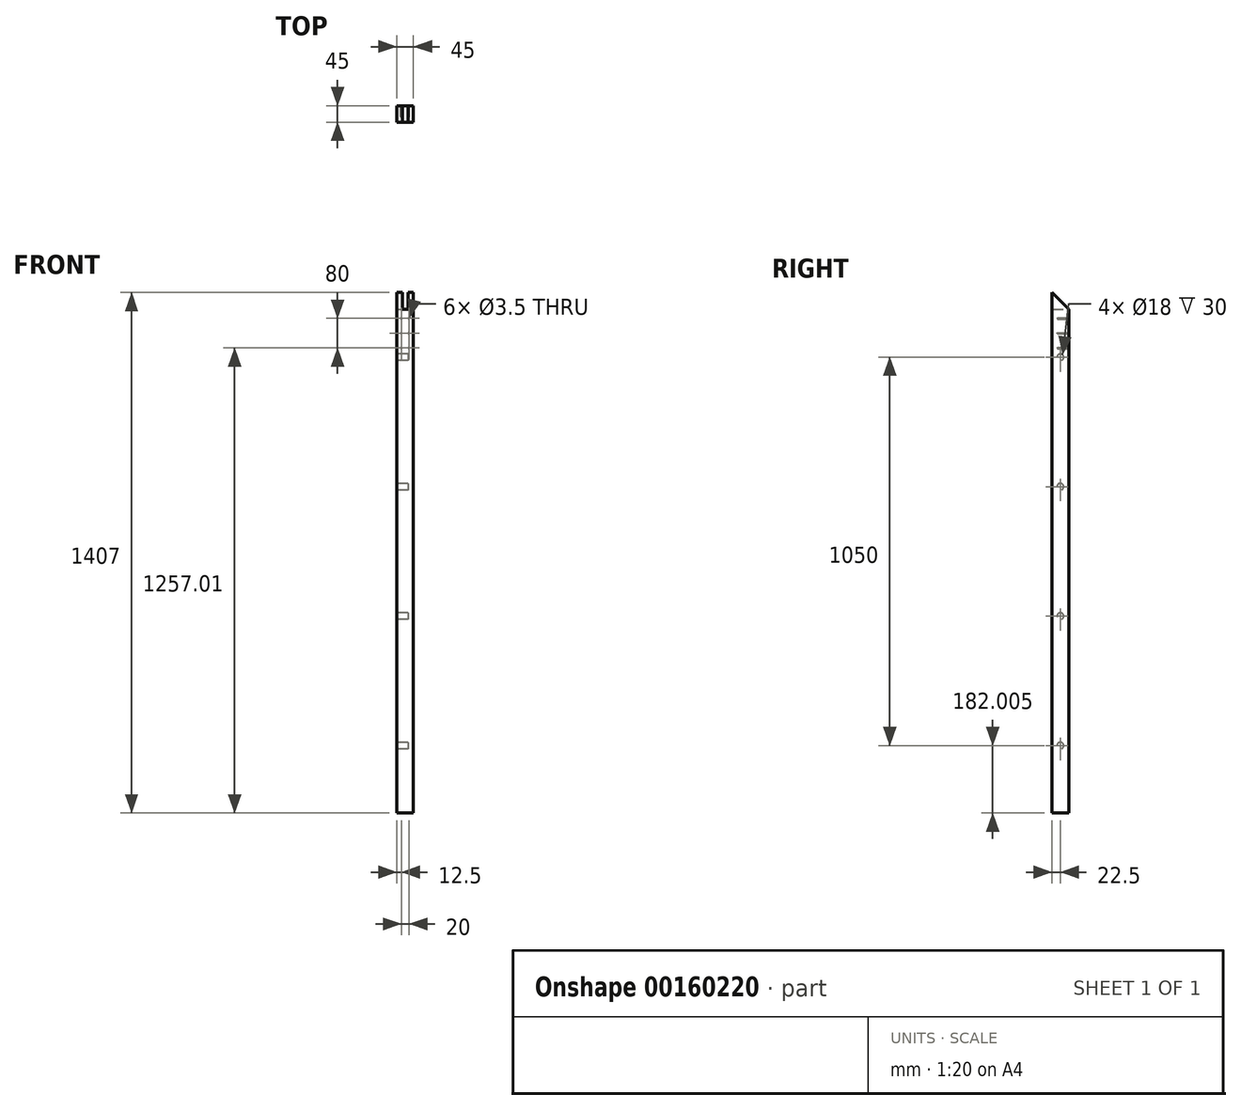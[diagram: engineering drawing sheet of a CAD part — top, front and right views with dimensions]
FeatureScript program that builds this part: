
annotation { "Feature Type Name" : "Feature", "Feature Type Description" : "" }
export const myFeature = defineFeature(function(context is Context, id is Id, definition is map)
    precondition{}
    {
        {
            var Q0;
            Q0=qCreatedBy(makeId("Front.planeOp"),FACE);
            var sketch = newSketch(context, id + "F0", { "sketchPlane" : qUnion([Q0])});
            skLineSegment(sketch, "E0.bottom", {"start": v(-22.5, 213.33) * mm, "end": v(22.5, 213.33) * mm});
            skLineSegment(sketch, "E0.top", {"start": v(-22.5, -1193.67) * mm, "end": v(22.5, -1193.67) * mm});
            skLineSegment(sketch, "E0.left", {"start": v(-22.5, 213.33) * mm, "end": v(-22.5, -1193.67) * mm});
            skLineSegment(sketch, "E0.right", {"start": v(22.5, 213.33) * mm, "end": v(22.5, -1193.67) * mm});
            skSolve(sketch);
        }
        {
            var Q0;
            Q0=makeQuery(id+"F0.imprint","IMPRINT",FACE,{"disambiguationData":[TD([[makeQuery(id+"F0.imprint","IMPRINT",EDGE,{"derivedFrom":sQuery(id+"F0.wireOp",EDGE,"E0.bottom")}),-1.0]])]});
            extrude(context, id + "F1", {"entities" : qUnion([Q0]), "endBound" : BoundingType.SYMMETRIC, "depth" : 45 * mm});
        }
        {
            var Q0;
            Q0=makeQuery(id+"F1.opExtrude","SWEPT_FACE",FACE,{"disambiguationData":[OSD([sQuery(id+"F0.wireOp",EDGE,"E0.bottom")])]});
            var sketch = newSketch(context, id + "F2", { "sketchPlane" : qUnion([Q0])});
            skLineSegment(sketch, "E1.bottom", {"start": v(7.5, -22.5) * mm, "end": v(22.5, -22.5) * mm});
            skLineSegment(sketch, "E1.top", {"start": v(7.5, 22.5) * mm, "end": v(22.5, 22.5) * mm});
            skLineSegment(sketch, "E1.left", {"start": v(7.5, -22.5) * mm, "end": v(7.5, 22.5) * mm});
            skLineSegment(sketch, "E1.right", {"start": v(22.5, -22.5) * mm, "end": v(22.5, 22.5) * mm});
            skLineSegment(sketch, "E2.bottom", {"start": v(-7.5, -22.5) * mm, "end": v(-22.5, -22.5) * mm});
            skLineSegment(sketch, "E2.top", {"start": v(-7.5, 22.5) * mm, "end": v(-22.5, 22.5) * mm});
            skLineSegment(sketch, "E2.left", {"start": v(-7.5, -22.5) * mm, "end": v(-7.5, 22.5) * mm});
            skLineSegment(sketch, "E2.right", {"start": v(-22.5, -22.5) * mm, "end": v(-22.5, 22.5) * mm});
            skSolve(sketch);
        }
        {
            var Q0;
            Q0=makeQuery(id+"F1.opExtrude","CAP_EDGE",EDGE,{"disambiguationData":[OSD([sQuery(id+"F0.wireOp",EDGE,"E0.bottom")])],"isStart":true});
            chamfer(context, id + "F3", {"entities" : qUnion([Q0]), "chamferType" : ChamferType.OFFSET_ANGLE, "width" : 45 * mm, "oppositeDirection" : false, "angle" : 45 * degree, "tangentPropagation" : true});
        }
        {
            var Q0;
            {var subQ0=sQuery(id+"F2.wireOp",EDGE,"E1.left");Q0=makeQuery(id+"F2.imprint","IMPRINT",FACE,{"disambiguationData":[TD([[makeQuery(id+"F2.imprint","IMPRINT",EDGE,{"derivedFrom":subQ0}),1.0]])]});}
            extrude(context, id + "F4", {"entities" : qUnion([Q0]), "operationType" : NewBodyOperationType.REMOVE, "oppositeDirection" : true, "depth" : 45 * mm});
        }
        {
            var Q0;
            Q0=makeQuery(id+"F1.opExtrude","SWEPT_FACE",FACE,{"disambiguationData":[OSD([sQuery(id+"F0.wireOp",EDGE,"E0.left")])]});
            var sketch = newSketch(context, id + "F5", { "sketchPlane" : qUnion([Q0])});
            skCircle(sketch, "E3", {"center": v(0, 38.33) * mm, "radius": 9 * mm});
            skCircle(sketch, "E4", {"center": v(0, -311.67) * mm, "radius": 9 * mm});
            skCircle(sketch, "E5", {"center": v(0, -661.67) * mm, "radius": 9 * mm});
            skCircle(sketch, "E6", {"center": v(0, -1011.67) * mm, "radius": 9 * mm});
            skSolve(sketch);
        }
        {
            var Q0;
            Q0=makeQuery(id+"F5.imprint","IMPRINT",FACE,{"disambiguationData":[TD([[makeQuery(id+"F5.imprint","IMPRINT",EDGE,{"derivedFrom":sQuery(id+"F5.wireOp",EDGE,"E3")}),1.0]])]});
            var Q1;
            Q1=makeQuery(id+"F5.imprint","IMPRINT",FACE,{"disambiguationData":[TD([[makeQuery(id+"F5.imprint","IMPRINT",EDGE,{"derivedFrom":sQuery(id+"F5.wireOp",EDGE,"E4")}),1.0]])]});
            var Q2;
            Q2=makeQuery(id+"F5.imprint","IMPRINT",FACE,{"disambiguationData":[TD([[makeQuery(id+"F5.imprint","IMPRINT",EDGE,{"derivedFrom":sQuery(id+"F5.wireOp",EDGE,"E5")}),1.0]])]});
            var Q3;
            Q3=makeQuery(id+"F5.imprint","IMPRINT",FACE,{"disambiguationData":[TD([[makeQuery(id+"F5.imprint","IMPRINT",EDGE,{"derivedFrom":sQuery(id+"F5.wireOp",EDGE,"E6")}),1.0]])]});
            extrude(context, id + "F6", {"entities" : qUnion([Q0, Q1, Q2, Q3]), "operationType" : NewBodyOperationType.REMOVE, "oppositeDirection" : true, "depth" : 30 * mm});
        }
        {
            var Q0;
            Q0=makeQuery(id+"F1.opExtrude","CAP_FACE",FACE,{"disambiguationData":[OSD([sQuery(id+"F0.wireOp",EDGE,"E0.bottom"),sQuery(id+"F0.wireOp",EDGE,"E0.top"),sQuery(id+"F0.wireOp",EDGE,"E0.left"),sQuery(id+"F0.wireOp",EDGE,"E0.right")])],"isStart":true});
            var sketch = newSketch(context, id + "F7", { "sketchPlane" : qUnion([Q0])});
            skPoint(sketch, "E7", {"position": v(22.5, -1193.67) * mm});
            skPoint(sketch, "E8", {"position": v(22.5, 168.33) * mm});
            skSolve(sketch);
        }
        {
            var Q0;
            {var subQ6=sQuery(id+"F0.wireOp",EDGE,"E0.top");Q0=makeQuery(id+"F7.imprint","IMPRINT",FACE,{"disambiguationData":[TD([[makeQuery(id+"F7.imprint","IMPRINT",EDGE,{"derivedFrom":makeQuery(id+"F1.opExtrude","CAP_EDGE",EDGE,{"disambiguationData":[OSD([subQ6])],"isStart":true})}),-1.0]])]});}
            var sketch = newSketch(context, id + "F8", { "sketchPlane" : qUnion([Q0])});
            skPoint(sketch, "E9", {"position": v(-10, 143.33) * mm});
            skPoint(sketch, "E10", {"position": v(-10, 103.33) * mm});
            skPoint(sketch, "E11", {"position": v(-10, 63.33) * mm});
            skPoint(sketch, "E12", {"position": v(10, 143.33) * mm});
            skPoint(sketch, "E13", {"position": v(10, 103.33) * mm});
            skPoint(sketch, "E14", {"position": v(10, 63.33) * mm});
            skSolve(sketch);
        }
        {
            var Q0;
            Q0=sQuery(id+"F8.wireOp",VERTEX,"E10");
            var Q1;
            Q1=sQuery(id+"F8.wireOp",VERTEX,"E11");
            var Q2;
            Q2=sQuery(id+"F8.wireOp",VERTEX,"E14");
            var Q3;
            Q3=sQuery(id+"F8.wireOp",VERTEX,"E13");
            var Q4;
            Q4=sQuery(id+"F8.wireOp",VERTEX,"E12");
            var Q5;
            Q5=sQuery(id+"F8.wireOp",VERTEX,"E9");
            var Q6;
            Q6=makeQuery(id+"F1.opExtrude","SWEPT_BODY",BODY,{"disambiguationData":[OSD([sQuery(id+"F0.wireOp",EDGE,"E0.bottom"),sQuery(id+"F0.wireOp",EDGE,"E0.top"),sQuery(id+"F0.wireOp",EDGE,"E0.left"),sQuery(id+"F0.wireOp",EDGE,"E0.right")])]});
            hole(context, id + "F9", {"style" : HoleStyle.SIMPLE, "endStyle" : HoleEndStyle.BLIND, "holeDiameter" : 3.5 * mm, "holeDepth" : 30 * mm, "startFromSketch" : true, "locations" : qUnion([Q0, Q1, Q2, Q3, Q4, Q5]), "scope" : qUnion([Q6])});
        }
    });
